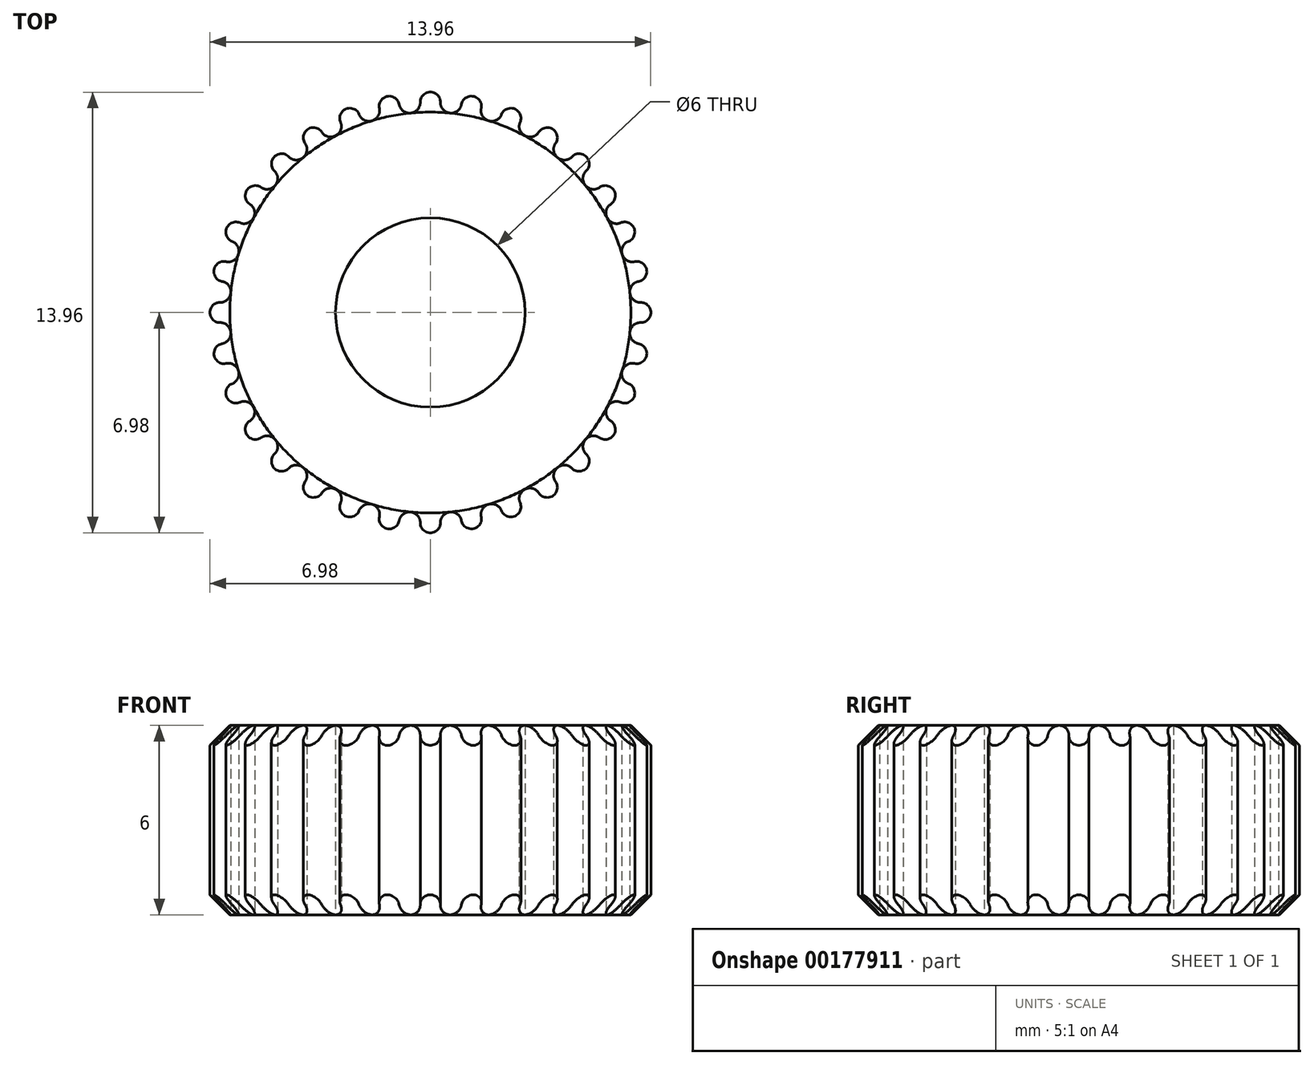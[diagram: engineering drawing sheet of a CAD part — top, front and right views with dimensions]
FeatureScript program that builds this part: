
annotation { "Feature Type Name" : "Feature", "Feature Type Description" : "" }
export const myFeature = defineFeature(function(context is Context, id is Id, definition is map)
    precondition{}
    {
        {
            var Q0;
            Q0=qCreatedBy(makeId("Top.planeOp"),FACE);
            var sketch = newSketch(context, id + "F0", { "sketchPlane" : qUnion([Q0])});
            skCircle(sketch, "E0", {"center": v(0, 0) * mm, "radius": 6.99 * mm, "construction": true});
            skCircle(sketch, "E1", {"center": v(0, 0) * mm, "radius": 6.35 * mm, "construction": true});
            skCircle(sketch, "E2", {"center": v(0, 0) * mm, "radius": 3 * mm, "construction": true});
            skSolve(sketch);
        }
        {
            var Q0;
            Q0=qCreatedBy(makeId("Top.planeOp"),FACE);
            var sketch = newSketch(context, id + "F1", { "sketchPlane" : qUnion([Q0])});
            skCircle(sketch, "E3.0", {"center": v(0, 0) * mm, "radius": 3 * mm});
            skLineSegment(sketch, "E4", {"start": v(0, 0) * mm, "end": v(0, 6.98) * mm, "construction": true});
            skArc(sketch, "E5", {"start": v(0.32, 6.66) * mm, "mid": v(0, 6.99) * mm, "end": v(-0.32, 6.66) * mm});
            skArc(sketch, "E6", {"start": v(-0.62, 6.32) * mm, "mid": v(-0.4, 6.43) * mm, "end": v(-0.32, 6.66) * mm});
            skArc(sketch, "E7", {"start": v(0.32, 6.66) * mm, "mid": v(0.4, 6.43) * mm, "end": v(0.62, 6.32) * mm});
            skLineSegment(sketch, "E8", {"start": v(-0.62, 6.32) * mm, "end": v(0, 0) * mm, "construction": true});
            skLineSegment(sketch, "E9", {"start": v(0.62, 6.32) * mm, "end": v(0, 0) * mm, "construction": true});
            skArc(sketch, "E10.1.0", {"start": v(-1.84, 6.08) * mm, "mid": v(-1.65, 6.23) * mm, "end": v(-1.61, 6.47) * mm});
            skArc(sketch, "E10.1.1", {"start": v(-0.99, 6.6) * mm, "mid": v(-1.36, 6.85) * mm, "end": v(-1.61, 6.47) * mm});
            skArc(sketch, "E10.1.2", {"start": v(-0.99, 6.6) * mm, "mid": v(-0.86, 6.39) * mm, "end": v(-0.62, 6.32) * mm});
            skArc(sketch, "E10.2.0", {"start": v(-3, 5.6) * mm, "mid": v(-2.83, 5.79) * mm, "end": v(-2.84, 6.03) * mm});
            skArc(sketch, "E10.2.1", {"start": v(-2.25, 6.28) * mm, "mid": v(-2.67, 6.45) * mm, "end": v(-2.84, 6.03) * mm});
            skArc(sketch, "E10.2.2", {"start": v(-2.25, 6.28) * mm, "mid": v(-2.09, 6.1) * mm, "end": v(-1.84, 6.08) * mm});
            skArc(sketch, "E10.3.0", {"start": v(-4.03, 4.9) * mm, "mid": v(-3.9, 5.12) * mm, "end": v(-3.97, 5.36) * mm});
            skArc(sketch, "E10.3.1", {"start": v(-3.43, 5.72) * mm, "mid": v(-3.88, 5.8) * mm, "end": v(-3.97, 5.36) * mm});
            skArc(sketch, "E10.3.2", {"start": v(-3.43, 5.72) * mm, "mid": v(-3.24, 5.57) * mm, "end": v(-3, 5.6) * mm});
            skArc(sketch, "E10.4.0", {"start": v(-4.9, 4.03) * mm, "mid": v(-4.83, 4.26) * mm, "end": v(-4.94, 4.48) * mm});
            skArc(sketch, "E10.4.1", {"start": v(-4.48, 4.94) * mm, "mid": v(-4.94, 4.94) * mm, "end": v(-4.94, 4.48) * mm});
            skArc(sketch, "E10.4.2", {"start": v(-4.48, 4.94) * mm, "mid": v(-4.26, 4.83) * mm, "end": v(-4.03, 4.9) * mm});
            skArc(sketch, "E10.5.0", {"start": v(-5.6, 3) * mm, "mid": v(-5.57, 3.24) * mm, "end": v(-5.72, 3.43) * mm});
            skArc(sketch, "E10.5.1", {"start": v(-5.36, 3.97) * mm, "mid": v(-5.8, 3.88) * mm, "end": v(-5.72, 3.43) * mm});
            skArc(sketch, "E10.5.2", {"start": v(-5.36, 3.97) * mm, "mid": v(-5.12, 3.9) * mm, "end": v(-4.9, 4.03) * mm});
            skArc(sketch, "E10.6.0", {"start": v(-6.08, 1.84) * mm, "mid": v(-6.1, 2.09) * mm, "end": v(-6.28, 2.25) * mm});
            skArc(sketch, "E10.6.1", {"start": v(-6.03, 2.84) * mm, "mid": v(-6.45, 2.67) * mm, "end": v(-6.28, 2.25) * mm});
            skArc(sketch, "E10.6.2", {"start": v(-6.03, 2.84) * mm, "mid": v(-5.79, 2.83) * mm, "end": v(-5.6, 3) * mm});
            skArc(sketch, "E10.7.0", {"start": v(-6.32, 0.62) * mm, "mid": v(-6.39, 0.86) * mm, "end": v(-6.6, 0.99) * mm});
            skArc(sketch, "E10.7.1", {"start": v(-6.47, 1.61) * mm, "mid": v(-6.85, 1.36) * mm, "end": v(-6.6, 0.99) * mm});
            skArc(sketch, "E10.7.2", {"start": v(-6.47, 1.61) * mm, "mid": v(-6.23, 1.65) * mm, "end": v(-6.08, 1.84) * mm});
            skArc(sketch, "E10.8.0", {"start": v(-6.32, -0.62) * mm, "mid": v(-6.43, -0.4) * mm, "end": v(-6.66, -0.32) * mm});
            skArc(sketch, "E10.8.1", {"start": v(-6.66, 0.32) * mm, "mid": v(-6.99, 0) * mm, "end": v(-6.66, -0.32) * mm});
            skArc(sketch, "E10.8.2", {"start": v(-6.66, 0.32) * mm, "mid": v(-6.43, 0.4) * mm, "end": v(-6.32, 0.62) * mm});
            skArc(sketch, "E10.9.0", {"start": v(-6.08, -1.84) * mm, "mid": v(-6.23, -1.65) * mm, "end": v(-6.47, -1.61) * mm});
            skArc(sketch, "E10.9.1", {"start": v(-6.6, -0.99) * mm, "mid": v(-6.85, -1.36) * mm, "end": v(-6.47, -1.61) * mm});
            skArc(sketch, "E10.9.2", {"start": v(-6.6, -0.99) * mm, "mid": v(-6.39, -0.86) * mm, "end": v(-6.32, -0.62) * mm});
            skArc(sketch, "E10.10.0", {"start": v(-5.6, -3) * mm, "mid": v(-5.79, -2.83) * mm, "end": v(-6.03, -2.84) * mm});
            skArc(sketch, "E10.10.1", {"start": v(-6.28, -2.25) * mm, "mid": v(-6.45, -2.67) * mm, "end": v(-6.03, -2.84) * mm});
            skArc(sketch, "E10.10.2", {"start": v(-6.28, -2.25) * mm, "mid": v(-6.1, -2.09) * mm, "end": v(-6.08, -1.84) * mm});
            skArc(sketch, "E10.11.0", {"start": v(-4.9, -4.03) * mm, "mid": v(-5.12, -3.9) * mm, "end": v(-5.36, -3.97) * mm});
            skArc(sketch, "E10.11.1", {"start": v(-5.72, -3.43) * mm, "mid": v(-5.8, -3.88) * mm, "end": v(-5.36, -3.97) * mm});
            skArc(sketch, "E10.11.2", {"start": v(-5.72, -3.43) * mm, "mid": v(-5.57, -3.24) * mm, "end": v(-5.6, -3) * mm});
            skArc(sketch, "E10.12.0", {"start": v(-4.03, -4.9) * mm, "mid": v(-4.26, -4.83) * mm, "end": v(-4.48, -4.94) * mm});
            skArc(sketch, "E10.12.1", {"start": v(-4.94, -4.48) * mm, "mid": v(-4.94, -4.94) * mm, "end": v(-4.48, -4.94) * mm});
            skArc(sketch, "E10.12.2", {"start": v(-4.94, -4.48) * mm, "mid": v(-4.83, -4.26) * mm, "end": v(-4.9, -4.03) * mm});
            skArc(sketch, "E10.13.0", {"start": v(-3, -5.6) * mm, "mid": v(-3.24, -5.57) * mm, "end": v(-3.43, -5.72) * mm});
            skArc(sketch, "E10.13.1", {"start": v(-3.97, -5.36) * mm, "mid": v(-3.88, -5.8) * mm, "end": v(-3.43, -5.72) * mm});
            skArc(sketch, "E10.13.2", {"start": v(-3.97, -5.36) * mm, "mid": v(-3.9, -5.12) * mm, "end": v(-4.03, -4.9) * mm});
            skArc(sketch, "E10.14.0", {"start": v(-1.84, -6.08) * mm, "mid": v(-2.09, -6.1) * mm, "end": v(-2.25, -6.28) * mm});
            skArc(sketch, "E10.14.1", {"start": v(-2.84, -6.03) * mm, "mid": v(-2.67, -6.45) * mm, "end": v(-2.25, -6.28) * mm});
            skArc(sketch, "E10.14.2", {"start": v(-2.84, -6.03) * mm, "mid": v(-2.83, -5.79) * mm, "end": v(-3, -5.6) * mm});
            skArc(sketch, "E10.15.0", {"start": v(-0.62, -6.32) * mm, "mid": v(-0.86, -6.39) * mm, "end": v(-0.99, -6.6) * mm});
            skArc(sketch, "E10.15.1", {"start": v(-1.61, -6.47) * mm, "mid": v(-1.36, -6.85) * mm, "end": v(-0.99, -6.6) * mm});
            skArc(sketch, "E10.15.2", {"start": v(-1.61, -6.47) * mm, "mid": v(-1.65, -6.23) * mm, "end": v(-1.84, -6.08) * mm});
            skArc(sketch, "E10.16.0", {"start": v(0.62, -6.32) * mm, "mid": v(0.4, -6.43) * mm, "end": v(0.32, -6.66) * mm});
            skArc(sketch, "E10.16.1", {"start": v(-0.32, -6.66) * mm, "mid": v(0, -6.99) * mm, "end": v(0.32, -6.66) * mm});
            skArc(sketch, "E10.16.2", {"start": v(-0.32, -6.66) * mm, "mid": v(-0.4, -6.43) * mm, "end": v(-0.62, -6.32) * mm});
            skArc(sketch, "E10.17.0", {"start": v(1.84, -6.08) * mm, "mid": v(1.65, -6.23) * mm, "end": v(1.61, -6.47) * mm});
            skArc(sketch, "E10.17.1", {"start": v(0.99, -6.6) * mm, "mid": v(1.36, -6.85) * mm, "end": v(1.61, -6.47) * mm});
            skArc(sketch, "E10.17.2", {"start": v(0.99, -6.6) * mm, "mid": v(0.86, -6.39) * mm, "end": v(0.62, -6.32) * mm});
            skArc(sketch, "E10.18.0", {"start": v(3, -5.6) * mm, "mid": v(2.83, -5.79) * mm, "end": v(2.84, -6.03) * mm});
            skArc(sketch, "E10.18.1", {"start": v(2.25, -6.28) * mm, "mid": v(2.67, -6.45) * mm, "end": v(2.84, -6.03) * mm});
            skArc(sketch, "E10.18.2", {"start": v(2.25, -6.28) * mm, "mid": v(2.09, -6.1) * mm, "end": v(1.84, -6.08) * mm});
            skArc(sketch, "E10.19.0", {"start": v(4.03, -4.9) * mm, "mid": v(3.9, -5.12) * mm, "end": v(3.97, -5.36) * mm});
            skArc(sketch, "E10.19.1", {"start": v(3.43, -5.72) * mm, "mid": v(3.88, -5.8) * mm, "end": v(3.97, -5.36) * mm});
            skArc(sketch, "E10.19.2", {"start": v(3.43, -5.72) * mm, "mid": v(3.24, -5.57) * mm, "end": v(3, -5.6) * mm});
            skArc(sketch, "E10.20.0", {"start": v(4.9, -4.03) * mm, "mid": v(4.83, -4.26) * mm, "end": v(4.94, -4.48) * mm});
            skArc(sketch, "E10.20.1", {"start": v(4.48, -4.94) * mm, "mid": v(4.94, -4.94) * mm, "end": v(4.94, -4.48) * mm});
            skArc(sketch, "E10.20.2", {"start": v(4.48, -4.94) * mm, "mid": v(4.26, -4.83) * mm, "end": v(4.03, -4.9) * mm});
            skArc(sketch, "E10.21.0", {"start": v(5.6, -3) * mm, "mid": v(5.57, -3.24) * mm, "end": v(5.72, -3.43) * mm});
            skArc(sketch, "E10.21.1", {"start": v(5.36, -3.97) * mm, "mid": v(5.8, -3.88) * mm, "end": v(5.72, -3.43) * mm});
            skArc(sketch, "E10.21.2", {"start": v(5.36, -3.97) * mm, "mid": v(5.12, -3.9) * mm, "end": v(4.9, -4.03) * mm});
            skArc(sketch, "E10.22.0", {"start": v(6.08, -1.84) * mm, "mid": v(6.1, -2.09) * mm, "end": v(6.28, -2.25) * mm});
            skArc(sketch, "E10.22.1", {"start": v(6.03, -2.84) * mm, "mid": v(6.45, -2.67) * mm, "end": v(6.28, -2.25) * mm});
            skArc(sketch, "E10.22.2", {"start": v(6.03, -2.84) * mm, "mid": v(5.79, -2.83) * mm, "end": v(5.6, -3) * mm});
            skArc(sketch, "E10.23.0", {"start": v(6.32, -0.62) * mm, "mid": v(6.39, -0.86) * mm, "end": v(6.6, -0.99) * mm});
            skArc(sketch, "E10.23.1", {"start": v(6.47, -1.61) * mm, "mid": v(6.85, -1.36) * mm, "end": v(6.6, -0.99) * mm});
            skArc(sketch, "E10.23.2", {"start": v(6.47, -1.61) * mm, "mid": v(6.23, -1.65) * mm, "end": v(6.08, -1.84) * mm});
            skArc(sketch, "E10.24.0", {"start": v(6.32, 0.62) * mm, "mid": v(6.43, 0.4) * mm, "end": v(6.66, 0.32) * mm});
            skArc(sketch, "E10.24.1", {"start": v(6.66, -0.32) * mm, "mid": v(6.99, 0) * mm, "end": v(6.66, 0.32) * mm});
            skArc(sketch, "E10.24.2", {"start": v(6.66, -0.32) * mm, "mid": v(6.43, -0.4) * mm, "end": v(6.32, -0.62) * mm});
            skArc(sketch, "E10.25.0", {"start": v(6.08, 1.84) * mm, "mid": v(6.23, 1.65) * mm, "end": v(6.47, 1.61) * mm});
            skArc(sketch, "E10.25.1", {"start": v(6.6, 0.99) * mm, "mid": v(6.85, 1.36) * mm, "end": v(6.47, 1.61) * mm});
            skArc(sketch, "E10.25.2", {"start": v(6.6, 0.99) * mm, "mid": v(6.39, 0.86) * mm, "end": v(6.32, 0.62) * mm});
            skArc(sketch, "E10.26.0", {"start": v(5.6, 3) * mm, "mid": v(5.79, 2.83) * mm, "end": v(6.03, 2.84) * mm});
            skArc(sketch, "E10.26.1", {"start": v(6.28, 2.25) * mm, "mid": v(6.45, 2.67) * mm, "end": v(6.03, 2.84) * mm});
            skArc(sketch, "E10.26.2", {"start": v(6.28, 2.25) * mm, "mid": v(6.1, 2.09) * mm, "end": v(6.08, 1.84) * mm});
            skArc(sketch, "E10.27.0", {"start": v(4.9, 4.03) * mm, "mid": v(5.12, 3.9) * mm, "end": v(5.36, 3.97) * mm});
            skArc(sketch, "E10.27.1", {"start": v(5.72, 3.43) * mm, "mid": v(5.8, 3.88) * mm, "end": v(5.36, 3.97) * mm});
            skArc(sketch, "E10.27.2", {"start": v(5.72, 3.43) * mm, "mid": v(5.57, 3.24) * mm, "end": v(5.6, 3) * mm});
            skArc(sketch, "E10.28.0", {"start": v(4.03, 4.9) * mm, "mid": v(4.26, 4.83) * mm, "end": v(4.48, 4.94) * mm});
            skArc(sketch, "E10.28.1", {"start": v(4.94, 4.48) * mm, "mid": v(4.94, 4.94) * mm, "end": v(4.48, 4.94) * mm});
            skArc(sketch, "E10.28.2", {"start": v(4.94, 4.48) * mm, "mid": v(4.83, 4.26) * mm, "end": v(4.9, 4.03) * mm});
            skArc(sketch, "E10.29.0", {"start": v(3, 5.6) * mm, "mid": v(3.24, 5.57) * mm, "end": v(3.43, 5.72) * mm});
            skArc(sketch, "E10.29.1", {"start": v(3.97, 5.36) * mm, "mid": v(3.88, 5.8) * mm, "end": v(3.43, 5.72) * mm});
            skArc(sketch, "E10.29.2", {"start": v(3.97, 5.36) * mm, "mid": v(3.9, 5.12) * mm, "end": v(4.03, 4.9) * mm});
            skArc(sketch, "E10.30.0", {"start": v(1.84, 6.08) * mm, "mid": v(2.09, 6.1) * mm, "end": v(2.25, 6.28) * mm});
            skArc(sketch, "E10.30.1", {"start": v(2.84, 6.03) * mm, "mid": v(2.67, 6.45) * mm, "end": v(2.25, 6.28) * mm});
            skArc(sketch, "E10.30.2", {"start": v(2.84, 6.03) * mm, "mid": v(2.83, 5.79) * mm, "end": v(3, 5.6) * mm});
            skArc(sketch, "E10.31.0", {"start": v(0.62, 6.32) * mm, "mid": v(0.86, 6.39) * mm, "end": v(0.99, 6.6) * mm});
            skArc(sketch, "E10.31.1", {"start": v(1.61, 6.47) * mm, "mid": v(1.36, 6.85) * mm, "end": v(0.99, 6.6) * mm});
            skArc(sketch, "E10.31.2", {"start": v(1.61, 6.47) * mm, "mid": v(1.65, 6.23) * mm, "end": v(1.84, 6.08) * mm});
            skArc(sketch, "E11", {"start": v(0.32, 6.66) * mm, "mid": v(0, 6.67) * mm, "end": v(-0.32, 6.66) * mm, "construction": true});
            skSolve(sketch);
        }
        {
            var Q0;
            Q0=makeQuery(id+"F1.imprint","IMPRINT",FACE,{"disambiguationData":[TD([[makeQuery(id+"F1.imprint","IMPRINT",EDGE,{"derivedFrom":sQuery(id+"F1.wireOp",EDGE,"E3.0")}),-1.0]])]});
            extrude(context, id + "F2", {"entities" : qUnion([Q0]), "depth" : 6 * mm});
        }
        {
            var Q0;
            Q0=qCreatedBy(makeId("Right.planeOp"),FACE);
            var sketch = newSketch(context, id + "F3", { "sketchPlane" : qUnion([Q0])});
            skLineSegment(sketch, "E12", {"start": v(6.99, 0) * mm, "end": v(6.99, 0.64) * mm});
            skLineSegment(sketch, "E13", {"start": v(6.99, 0.64) * mm, "end": v(6.35, 0) * mm});
            skLineSegment(sketch, "E14", {"start": v(6.35, 0) * mm, "end": v(6.99, 0) * mm});
            skLineSegment(sketch, "E15", {"start": v(7.04, 3) * mm, "end": v(-6.97, 3) * mm});
            skLineSegment(sketch, "E16.MirrorCS", {"start": v(6.35, 6) * mm, "end": v(6.99, 6) * mm});
            skLineSegment(sketch, "E17.MirrorCS", {"start": v(6.99, 5.37) * mm, "end": v(6.35, 6) * mm});
            skLineSegment(sketch, "E18.MirrorCS", {"start": v(6.99, 6) * mm, "end": v(6.99, 5.37) * mm});
            skSolve(sketch);
        }
        {
            var Q0;
            Q0 = qSketchRegion(id + "F3", true);
            var Q1;
            Q1=makeQuery(id+"F2.opExtrude","CAP_EDGE",EDGE,{"disambiguationData":[OSD([sQuery(id+"F1.wireOp",EDGE,"E3.0")])],"isStart":false});
            revolve(context, id + "F4", {"operationType" : NewBodyOperationType.REMOVE, "entities" : qUnion([Q0]), "axis" : qUnion([Q1]), "revolveType" : RevolveType.FULL});
        }
    });
